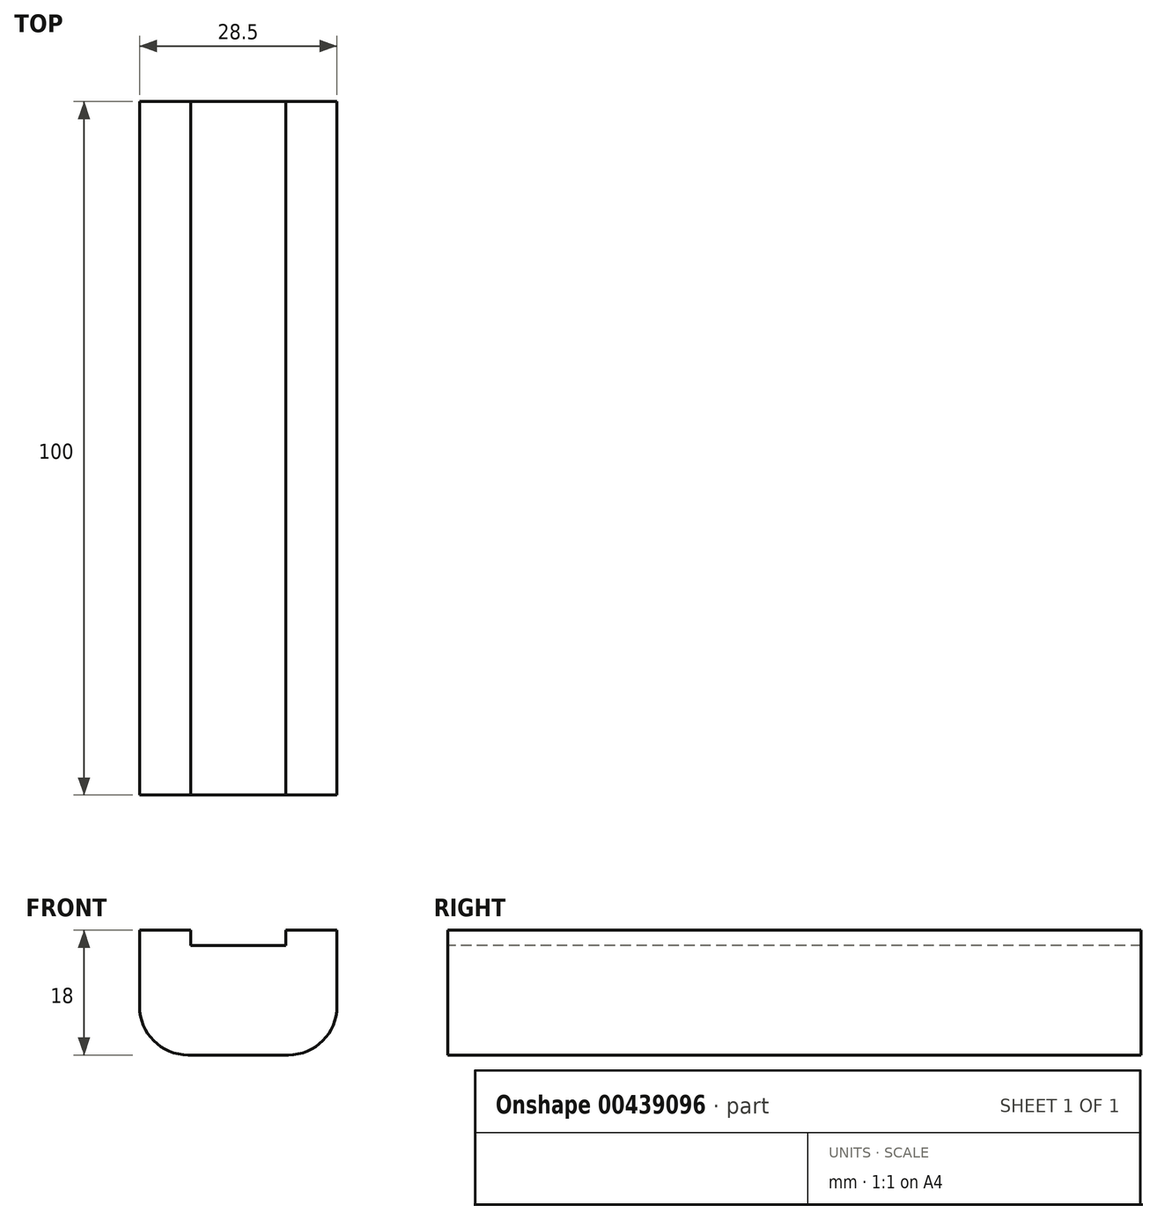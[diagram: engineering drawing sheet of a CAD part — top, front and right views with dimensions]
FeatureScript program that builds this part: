
annotation { "Feature Type Name" : "Feature", "Feature Type Description" : "" }
export const myFeature = defineFeature(function(context is Context, id is Id, definition is map)
    precondition{}
    {
        {
            var Q0;
            Q0=qCreatedBy(makeId("Front.planeOp"),FACE);
            var sketch = newSketch(context, id + "F0", { "sketchPlane" : qUnion([Q0])});
            skLineSegment(sketch, "E0", {"start": v(0, 0) * mm, "end": v(7.4, 0) * mm});
            skLineSegment(sketch, "E1", {"start": v(7.4, 0) * mm, "end": v(7.4, -2.2) * mm});
            skLineSegment(sketch, "E2", {"start": v(7.4, -2.2) * mm, "end": v(21.1, -2.2) * mm});
            skLineSegment(sketch, "E3", {"start": v(21.1, -2.2) * mm, "end": v(21.1, 0) * mm});
            skLineSegment(sketch, "E4", {"start": v(21.1, 0) * mm, "end": v(28.5, 0) * mm});
            skLineSegment(sketch, "E5", {"start": v(28.5, 0) * mm, "end": v(28.5, -11) * mm});
            skLineSegment(sketch, "E6", {"start": v(21.5, -18) * mm, "end": v(7, -18) * mm});
            skLineSegment(sketch, "E7", {"start": v(0, -11) * mm, "end": v(0, 0) * mm});
            skPoint(sketch, "E8.visualSharp", {"position": v(0, -18) * mm});
            skArc(sketch, "E8.filletArc", {"start": v(0, -11) * mm, "mid": v(2.05, -15.95) * mm, "end": v(7, -18) * mm});
            skPoint(sketch, "E9.visualSharp", {"position": v(28.5, -18) * mm});
            skArc(sketch, "E9.filletArc", {"start": v(21.5, -18) * mm, "mid": v(26.45, -15.95) * mm, "end": v(28.5, -11) * mm});
            skSolve(sketch);
        }
        {
            var Q0;
            Q0=makeQuery(id+"F0.imprint","IMPRINT",FACE,{"disambiguationData":[TD([[makeQuery(id+"F0.imprint","IMPRINT",EDGE,{"derivedFrom":sQuery(id+"F0.wireOp",EDGE,"E0")}),-1.0]])]});
            extrude(context, id + "F1", {"entities" : qUnion([Q0]), "oppositeDirection" : true, "depth" : 100 * mm});
        }
    });
